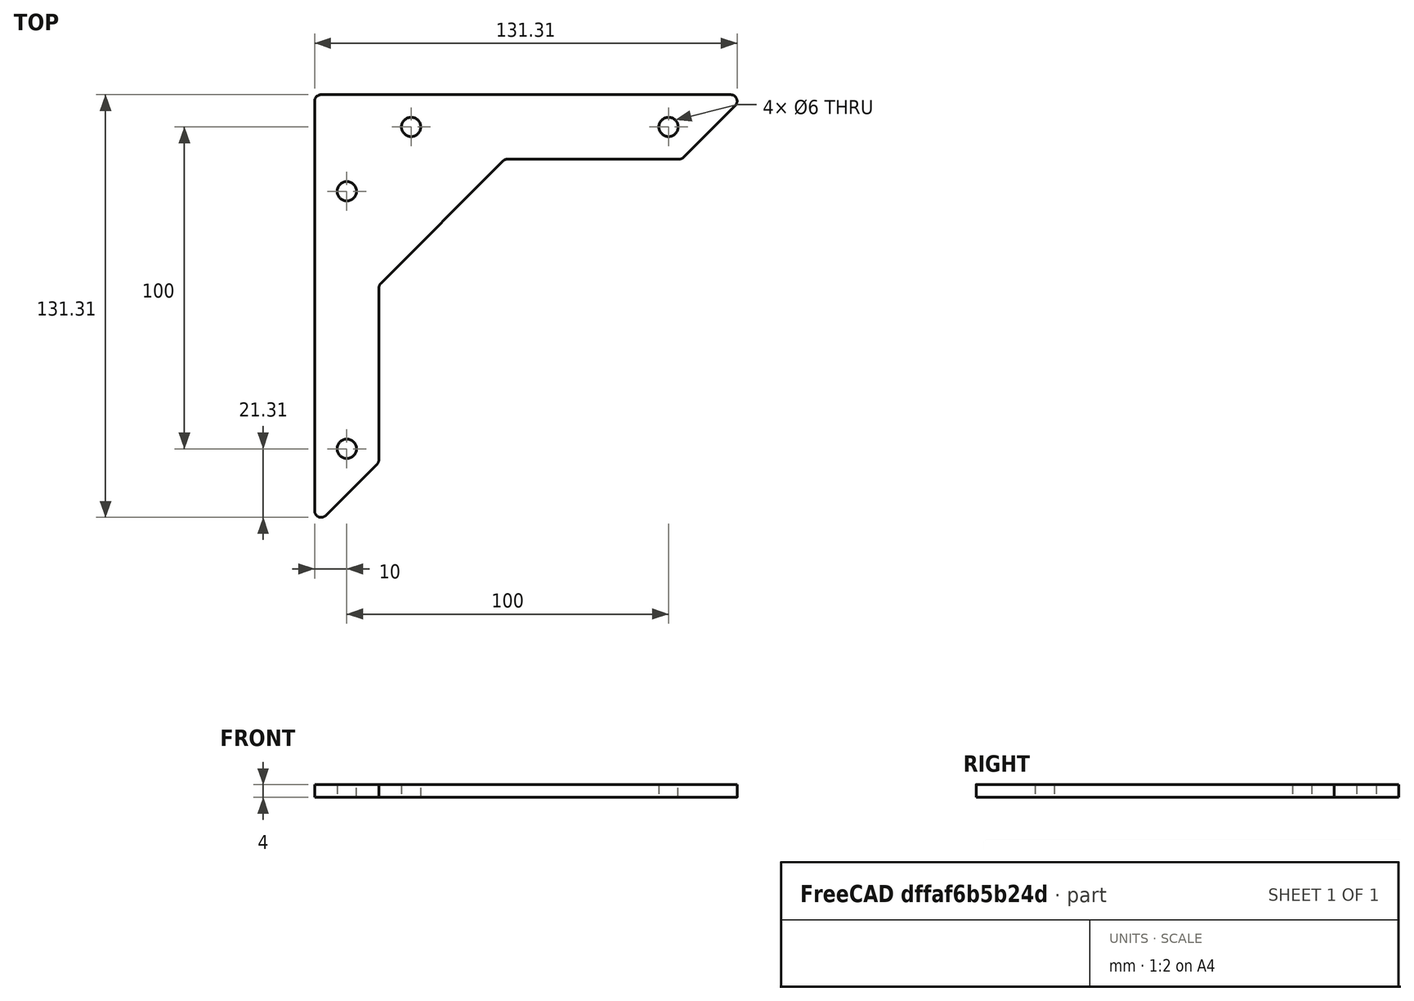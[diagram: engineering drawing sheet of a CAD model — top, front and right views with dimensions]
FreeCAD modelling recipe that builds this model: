
FCSTD DOCUMENT  (FreeCAD 0.19R24267 +99 (Git))
Label: V2 Enclosure ends right angle bracket
License: All rights reserved
LicenseURL: http://en.wikipedia.org/wiki/All_rights_reserved
objects: Sketcher::SketchObject×1, PartDesign::Pad×1, PartDesign::Body×1
note: 4 computed .brp shape members not serialized (recipe doc carries the construction recipe); baked Part::Feature solids carry a one-line shape summary decoded from their .brp

FEATURE [Sketcher::SketchObject] Sketch
  FullyConstrained = true
  MapMode = 5
  Support = -> [XY_Plane]
  sketch-geometry (24):
    g0: LineSegment StartX=2 StartY=0 StartZ=0 EndX=129.314 EndY=0 EndZ=0
    g1: LineSegment StartX=0 StartY=-129.314 StartZ=0 EndX=0 EndY=-2 EndZ=0
    g2: LineSegment StartX=3.41421 StartY=-130.728 StartZ=0 EndX=19.4142 EndY=-114.728 EndZ=0
    g3: LineSegment StartX=10 StartY=0 StartZ=0 EndX=10 EndY=-124.142 EndZ=0
    g4: LineSegment StartX=0 StartY=-10 StartZ=0 EndX=124.142 EndY=-10 EndZ=0
    g5: Circle CenterX=10 CenterY=-110 CenterZ=0 NormalX=0 NormalY=0 NormalZ=1 AngleXU=0 Radius=3
    g6: Circle CenterX=110 CenterY=-10 CenterZ=0 NormalX=0 NormalY=0 NormalZ=1 AngleXU=0 Radius=3
    g7: Circle CenterX=10 CenterY=-30 CenterZ=0 NormalX=0 NormalY=0 NormalZ=1 AngleXU=0 Radius=3
    g8: Circle CenterX=30 CenterY=-10 CenterZ=0 NormalX=0 NormalY=0 NormalZ=1 AngleXU=0 Radius=3
    g9: ArcOfCircle CenterX=2 CenterY=-129.314 CenterZ=0 NormalX=0 NormalY=0 NormalZ=1 AngleXU=0 Radius=2 StartAngle=3.14159 EndAngle=5.49779
    g10: ArcOfCircle CenterX=2 CenterY=-2 CenterZ=0 NormalX=0 NormalY=0 NormalZ=1 AngleXU=0 Radius=2 StartAngle=1.5708 EndAngle=3.14159
    g11: ArcOfCircle CenterX=129.314 CenterY=-2 CenterZ=0 NormalX=0 NormalY=0 NormalZ=1 AngleXU=0 Radius=2 StartAngle=5.49779 EndAngle=7.85398
    g12: Circle CenterX=110 CenterY=-10 CenterZ=0 NormalX=0 NormalY=0 NormalZ=1 AngleXU=0 Radius=10
    g13: LineSegment StartX=113.314 StartY=-20 StartZ=0 EndX=60 EndY=-20 EndZ=0
    g14: LineSegment StartX=20 StartY=-60 StartZ=0 EndX=20 EndY=-113.314 EndZ=0
    g15: LineSegment StartX=114.728 StartY=-19.4142 StartZ=0 EndX=130.728 EndY=-3.41421 EndZ=0
    g16: LineSegment StartX=58.5858 StartY=-20.5858 StartZ=0 EndX=20.5858 EndY=-58.5858 EndZ=0
    g17: LineSegment StartX=20 StartY=-60 StartZ=0 EndX=20 EndY=-20 EndZ=0
    g18: LineSegment StartX=60 StartY=-20 StartZ=0 EndX=20 EndY=-20 EndZ=0
    g19: ArcOfCircle CenterX=22 CenterY=-60 CenterZ=0 NormalX=0 NormalY=0 NormalZ=1 AngleXU=0 Radius=2 StartAngle=2.35619 EndAngle=3.14159
    g20: ArcOfCircle CenterX=60 CenterY=-22 CenterZ=0 NormalX=0 NormalY=0 NormalZ=1 AngleXU=0 Radius=2 StartAngle=1.5708 EndAngle=2.35619
    g21: ArcOfCircle CenterX=113.314 CenterY=-18 CenterZ=0 NormalX=0 NormalY=0 NormalZ=1 AngleXU=0 Radius=2 StartAngle=4.71239 EndAngle=5.49779
    g22: ArcOfCircle CenterX=18 CenterY=-113.314 CenterZ=0 NormalX=0 NormalY=0 NormalZ=1 AngleXU=0 Radius=2 StartAngle=5.49779 EndAngle=6.28319
    g23: Circle CenterX=10 CenterY=-110 CenterZ=0 NormalX=0 NormalY=0 NormalZ=1 AngleXU=0 Radius=10
  constraints (65):
    c: Vertical(g1)
    c: Horizontal(g0)
    c: Equal(g0,g1)
    c: PointOnObject(g3,g0)
    c: PointOnObject(g3,g2)
    c: Vertical(g3)
    c: PointOnObject(g4,g1)
    c: PointOnObject(g4,g2)
    c: Horizontal(g4)
    c: DistanceX(g-1,g3) = 10
    c: DistanceY(g4,g-1) = 10
    c: PointOnObject(g5,g3)
    c: PointOnObject(g6,g4)
    c: DistanceY(g5,g4) = 100
    c: DistanceX(g3,g6) = 100
    c: PointOnObject(g7,g3)
    c: PointOnObject(g8,g4)
    c: DistanceX(g3,g8) = 20
    c: DistanceY(g7,g4) = 20
    c: Equal(g5,g7)
    c: Equal(g7,g8)
    c: Equal(g8,g6)
    c: Radius(g5) = 3
    c: Tangent(g1,g9) = 1.5708
    c: Tangent(g2,g9) = -1.5708
    c: Tangent(g1,g10) = 1.5708
    c: Tangent(g0,g10) = 1.5708
    c: Tangent(g0,g11) = 1.5708
    c: Equal(g9,g11)
    c: Equal(g11,g10)
    c: Radius(g10) = 2
    c: PointOnObject(g0,g-1)
    c: PointOnObject(g1,g-2)
    c: Coincident(g12,g6)
    c: Tangent(g12,g0)
    c: Tangent(g12,g2)
    c: Horizontal(g13)
    c: Vertical(g14)
    c: Tangent(g2,g15)
    c: Vertical(g17)
    c: Coincident(g18,g17)
    c: Horizontal(g18)
    c: Equal(g18,g17)
    c: DistanceX(g18,g18) = 40
    c: Tangent(g15,g11) = -1.5708
    c: Tangent(g16,g19) = -1.5708
    c: Tangent(g14,g19) = -1.5708
    c: Tangent(g16,g20) = -1.5708
    c: Tangent(g13,g20) = -1.5708
    c: Tangent(g15,g21) = -1.5708
    c: Tangent(g13,g21) = 1.5708
    c: Tangent(g2,g22) = -1.5708
    c: Tangent(g14,g22) = 1.5708
    c: Equal(g22,g19)
    c: Equal(g19,g20)
    c: Equal(g20,g21)
    c: Equal(g21,g10)
    c: Coincident(g13,g18)
    c: Coincident(g17,g14)
    c: Tangent(g13,g12)
    c: Coincident(g23,g5)
    c: Tangent(g23,g1)
    c: Tangent(g23,g14)
    c: Angle(g2,g1) = 0.785398
    c: Angle(g0,g15) = 0.785398
FEATURE [PartDesign::Pad] Pad
  Direction = (1,1,1)
  Length = 4
  Length2 = 100
  Profile = -> Sketch
  Type = 0
FEATURE [PartDesign::Body] Body
  Group = -> [Sketch,Pad]
  Origin = -> Origin
  Tip = -> Pad
